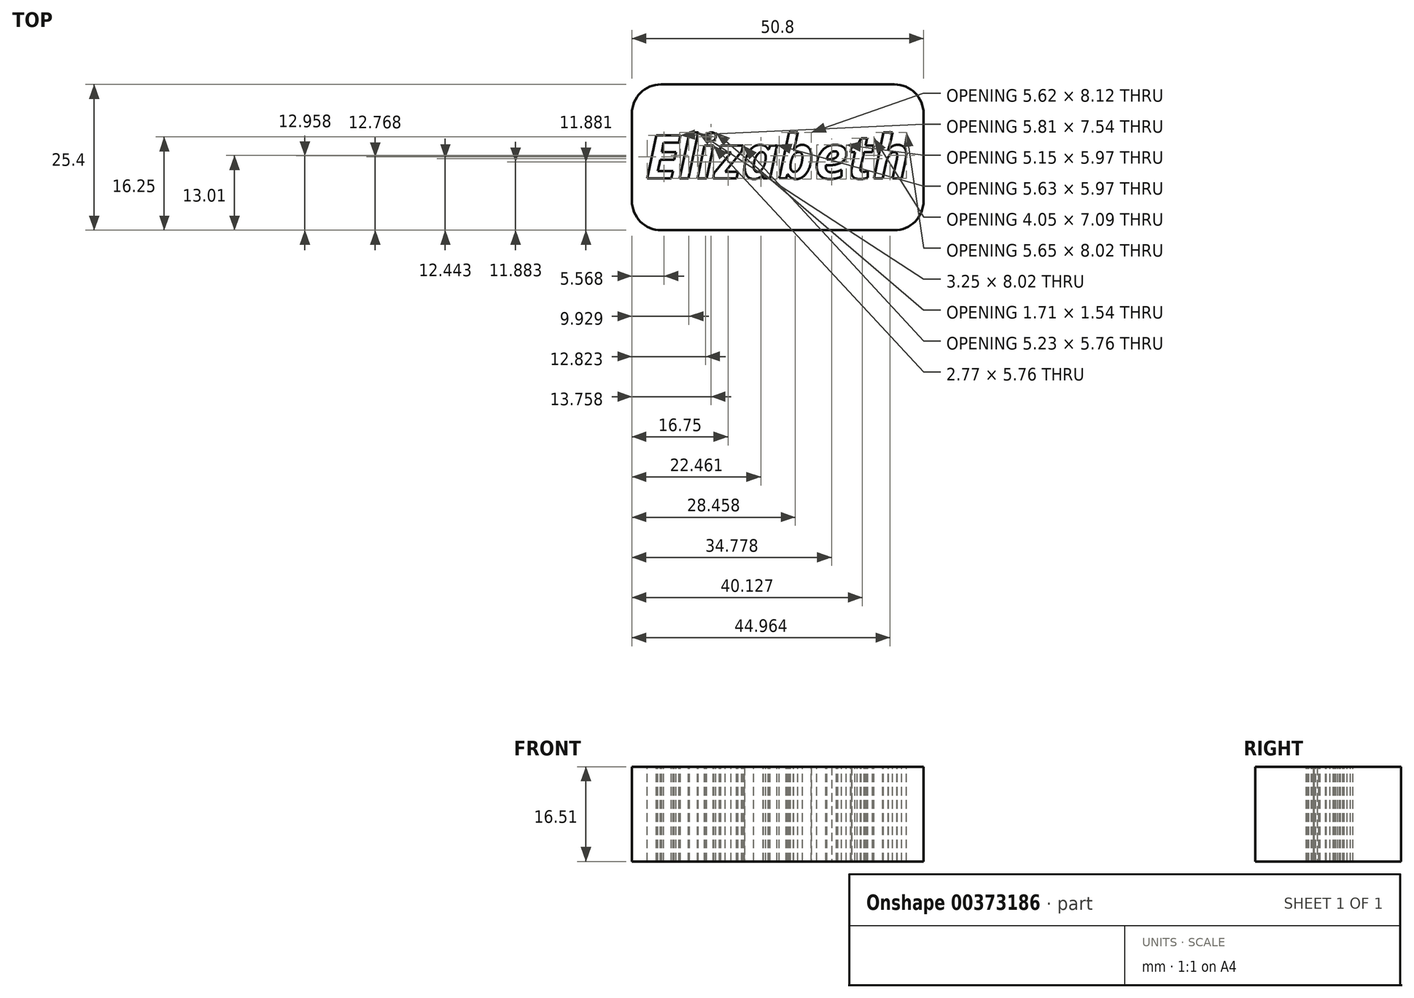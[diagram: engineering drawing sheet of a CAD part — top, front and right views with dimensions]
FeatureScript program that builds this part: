
annotation { "Feature Type Name" : "Feature", "Feature Type Description" : "" }
export const myFeature = defineFeature(function(context is Context, id is Id, definition is map)
    precondition{}
    {
        {
            var Q0;
            Q0=qCreatedBy(makeId("Top.planeOp"),FACE);
            var sketch = newSketch(context, id + "F0", { "sketchPlane" : qUnion([Q0])});
            skLineSegment(sketch, "E0", {"start": v(0, 0) * mm, "end": v(0, 25.4) * mm});
            skLineSegment(sketch, "E1", {"start": v(0, 25.4) * mm, "end": v(50.8, 25.4) * mm});
            skLineSegment(sketch, "E2", {"start": v(50.8, 25.4) * mm, "end": v(50.8, 0) * mm});
            skLineSegment(sketch, "E3", {"start": v(50.8, 0) * mm, "end": v(0, 0) * mm});
            skSolve(sketch);
        }
        {
            var Q0;
            Q0 = qSketchRegion(id + "F0", true);
            extrude(context, id + "F1", {"entities" : qUnion([Q0]), "depth" : 16.5 * mm});
        }
        {
            var Q0;
            Q0=makeQuery(id+"F1.opExtrude","CAP_FACE",FACE,{"disambiguationData":[OSD([sQuery(id+"F0.wireOp",EDGE,"E0"),sQuery(id+"F0.wireOp",EDGE,"E1"),sQuery(id+"F0.wireOp",EDGE,"E2"),sQuery(id+"F0.wireOp",EDGE,"E3")])],"isStart":false});
            var sketch = newSketch(context, id + "F2", { "sketchPlane" : qUnion([Q0])});
            skText(sketch, "E4", { "text": "Elizabeth", "fontName": "OpenSans-BoldItalic.ttf"});
            const initialGuessF2  = {"E4": [0.00239, 0.009, 1, 0, 0.0076]};
            skSetInitialGuess(sketch, initialGuessF2);
            skSolve(sketch);
        }
        {
            var Q0;
            Q0 = qSketchRegion(id + "F2", true);
            extrude(context, id + "F3", {"entities" : qUnion([Q0]), "operationType" : NewBodyOperationType.REMOVE, "oppositeDirection" : true, "depth" : 38.1 * mm});
        }
        {
            var Q0;
            Q0=makeQuery(id+"F1.opExtrude","SWEPT_EDGE",EDGE,{"disambiguationData":[OSD([sQuery(id+"F0.wireOp",EDGE,"E0"),sQuery(id+"F0.wireOp",EDGE,"E3")])]});
            var Q1;
            Q1=makeQuery(id+"F1.opExtrude","SWEPT_EDGE",EDGE,{"disambiguationData":[OSD([sQuery(id+"F0.wireOp",EDGE,"E2"),sQuery(id+"F0.wireOp",EDGE,"E3")])]});
            var Q2;
            Q2=makeQuery(id+"F1.opExtrude","SWEPT_EDGE",EDGE,{"disambiguationData":[OSD([sQuery(id+"F0.wireOp",EDGE,"E1"),sQuery(id+"F0.wireOp",EDGE,"E2")])]});
            var Q3;
            Q3=makeQuery(id+"F1.opExtrude","SWEPT_EDGE",EDGE,{"disambiguationData":[OSD([sQuery(id+"F0.wireOp",EDGE,"E0"),sQuery(id+"F0.wireOp",EDGE,"E1")])]});
            fillet(context, id + "F4", {"entities" : qUnion([Q0, Q1, Q2, Q3]), "radius" : 5.08 * mm, "tangentPropagation" : true, "allowEdgeOverflow" : false});
        }
    });
